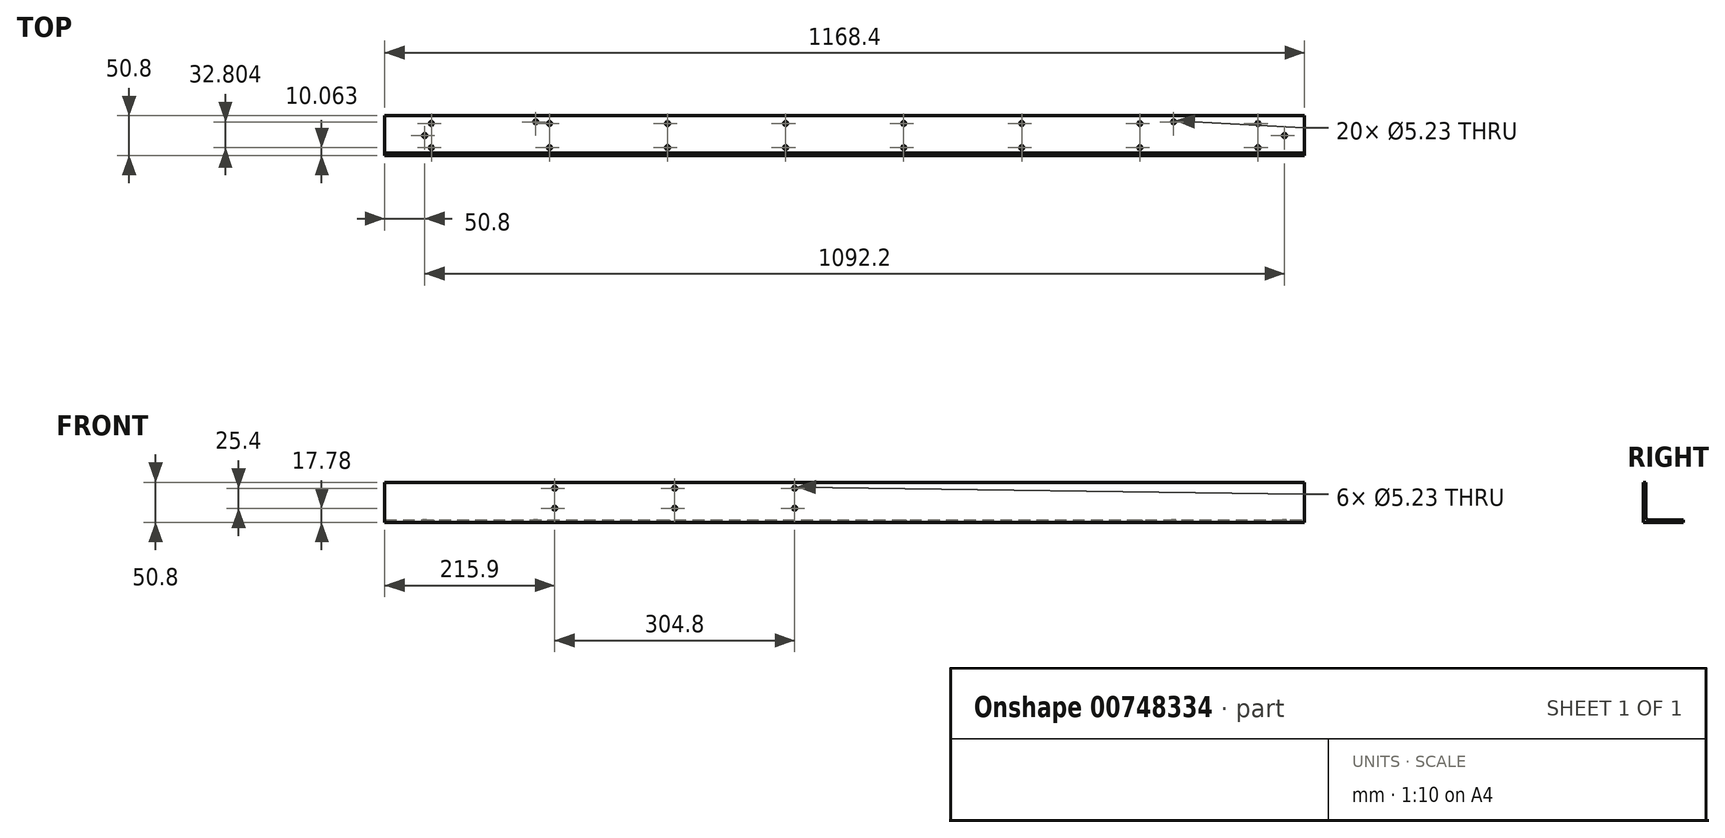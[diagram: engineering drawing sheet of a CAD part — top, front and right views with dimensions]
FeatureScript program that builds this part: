
annotation { "Feature Type Name" : "Feature", "Feature Type Description" : "" }
export const myFeature = defineFeature(function(context is Context, id is Id, definition is map)
    precondition{}
    {
        {
            var Q0;
            Q0=qCreatedBy(makeId("Right.planeOp"),FACE);
            var sketch = newSketch(context, id + "F0", { "sketchPlane" : qUnion([Q0])});
            skLineSegment(sketch, "E0", {"start": v(0, 0) * mm, "end": v(0, -44.45) * mm});
            skLineSegment(sketch, "E1", {"start": v(3.18, -47.62) * mm, "end": v(47.63, -47.62) * mm});
            skLineSegment(sketch, "E2.0", {"start": v(-3.18, -50.8) * mm, "end": v(47.63, -50.8) * mm});
            skLineSegment(sketch, "E2.1", {"start": v(-3.17, 0) * mm, "end": v(-3.18, -50.8) * mm});
            skLineSegment(sketch, "E3", {"start": v(-3.18, 0) * mm, "end": v(0, 0) * mm});
            skLineSegment(sketch, "E4", {"start": v(47.63, -47.62) * mm, "end": v(47.63, -50.8) * mm});
            skPoint(sketch, "E5.visualSharp", {"position": v(0, -47.63) * mm});
            skArc(sketch, "E5.filletArc", {"start": v(0, -44.45) * mm, "mid": v(0.93, -46.7) * mm, "end": v(3.18, -47.63) * mm});
            skSolve(sketch);
        }
        {
            var Q0;
            Q0=makeQuery(id+"F0.imprint","IMPRINT",FACE,{"disambiguationData":[TD([[makeQuery(id+"F0.imprint","IMPRINT",EDGE,{"derivedFrom":sQuery(id+"F0.wireOp",EDGE,"E0")}),-1.0]])]});
            extrude(context, id + "F1", {"entities" : qUnion([Q0]), "oppositeDirection" : true, "depth" : 1168.4 * mm, "offsetDistance" : 25.4 * mm});
        }
        {
            var Q0;
            Q0=makeQuery(id+"F1.opExtrude","SWEPT_FACE",FACE,{"disambiguationData":[OSD([sQuery(id+"F0.wireOp",EDGE,"E2.0")])]});
            var sketch = newSketch(context, id + "F2", { "sketchPlane" : qUnion([Q0])});
            skLineSegment(sketch, "E6", {"start": v(-584.2, -47.62) * mm, "end": v(-584.2, 3.17) * mm, "construction": true});
            skLineSegment(sketch, "E7", {"start": v(-1168.4, -22.22) * mm, "end": v(0, -22.22) * mm, "construction": true});
            skLineSegment(sketch, "E8.0", {"start": v(-1371.6, -37.57) * mm, "end": v(203.2, -37.57) * mm, "construction": true});
            skLineSegment(sketch, "E9.0", {"start": v(-1371.6, -6.88) * mm, "end": v(203.2, -6.88) * mm, "construction": true});
            skLineSegment(sketch, "E10.0", {"start": v(-509.2, -47.62) * mm, "end": v(-509.2, 3.17) * mm, "construction": true});
            skLineSegment(sketch, "E11.0", {"start": v(-359.2, -47.62) * mm, "end": v(-359.2, 3.17) * mm, "construction": true});
            skLineSegment(sketch, "E12.0", {"start": v(-209.2, -47.62) * mm, "end": v(-209.2, 3.17) * mm, "construction": true});
            skLineSegment(sketch, "E13.0", {"start": v(-59.2, -47.62) * mm, "end": v(-59.2, 3.17) * mm, "construction": true});
            skLineSegment(sketch, "E14.0", {"start": v(-659.2, -47.62) * mm, "end": v(-659.2, 3.17) * mm, "construction": true});
            skLineSegment(sketch, "E15.0", {"start": v(-809.2, -47.63) * mm, "end": v(-809.2, 3.17) * mm, "construction": true});
            skLineSegment(sketch, "E16.0", {"start": v(-959.2, -47.63) * mm, "end": v(-959.2, 3.17) * mm, "construction": true});
            skLineSegment(sketch, "E17.0", {"start": v(-1109.2, -47.63) * mm, "end": v(-1109.2, 3.17) * mm, "construction": true});
            skCircle(sketch, "E18", {"center": v(-1109.2, -37.57) * mm, "radius": 2.62 * mm});
            skCircle(sketch, "E19", {"center": v(-1109.2, -6.88) * mm, "radius": 2.62 * mm});
            skCircle(sketch, "E20", {"center": v(-959.2, -37.57) * mm, "radius": 2.62 * mm});
            skCircle(sketch, "E21", {"center": v(-959.2, -6.88) * mm, "radius": 2.62 * mm});
            skCircle(sketch, "E22", {"center": v(-809.2, -37.57) * mm, "radius": 2.62 * mm});
            skCircle(sketch, "E23", {"center": v(-809.2, -6.88) * mm, "radius": 2.62 * mm});
            skCircle(sketch, "E24", {"center": v(-659.2, -37.57) * mm, "radius": 2.62 * mm});
            skCircle(sketch, "E25", {"center": v(-659.2, -6.88) * mm, "radius": 2.62 * mm});
            skCircle(sketch, "E26", {"center": v(-509.2, -37.57) * mm, "radius": 2.62 * mm});
            skCircle(sketch, "E27", {"center": v(-509.2, -6.88) * mm, "radius": 2.62 * mm});
            skCircle(sketch, "E28", {"center": v(-359.2, -37.57) * mm, "radius": 2.62 * mm});
            skCircle(sketch, "E29", {"center": v(-359.2, -6.88) * mm, "radius": 2.62 * mm});
            skCircle(sketch, "E30", {"center": v(-209.2, -37.57) * mm, "radius": 2.62 * mm});
            skCircle(sketch, "E31", {"center": v(-209.2, -6.88) * mm, "radius": 2.62 * mm});
            skCircle(sketch, "E32", {"center": v(-59.2, -37.57) * mm, "radius": 2.62 * mm});
            skCircle(sketch, "E33", {"center": v(-59.2, -6.88) * mm, "radius": 2.62 * mm});
            skSolve(sketch);
        }
        {
            var Q0;
            Q0=qSketchRegion(id+"F2",true);
            extrude(context, id + "F3", {"entities" : qUnion([Q0]), "operationType" : NewBodyOperationType.REMOVE, "endBound" : BoundingType.THROUGH_ALL, "oppositeDirection" : true, "depth" : 25.4 * mm, "offsetDistance" : 25.4 * mm});
        }
        {
            var Q0;
            Q0=makeQuery(id+"F1.opExtrude","SWEPT_FACE",FACE,{"disambiguationData":[OSD([sQuery(id+"F0.wireOp",EDGE,"E1")])]});
            var sketch = newSketch(context, id + "F4", { "sketchPlane" : qUnion([Q0])});
            skLineSegment(sketch, "E34", {"start": v(-25.4, 47.63) * mm, "end": v(-25.4, 3.18) * mm, "construction": true});
            skCircle(sketch, "E35", {"center": v(-25.4, 22.23) * mm, "radius": 2.62 * mm});
            skLineSegment(sketch, "E36", {"start": v(-1117.6, 47.63) * mm, "end": v(-1117.6, 3.18) * mm, "construction": true});
            skCircle(sketch, "E37", {"center": v(-1117.6, 22.22) * mm, "radius": 2.62 * mm});
            skLineSegment(sketch, "E38", {"start": v(0, 22.23) * mm, "end": v(-1168.4, 22.22) * mm, "construction": true});
            skPoint(sketch, "E38.endSnap0", {"position": v(-1168.4, 25.4) * mm});
            skLineSegment(sketch, "E39", {"start": v(0, 39.69) * mm, "end": v(-1168.4, 39.69) * mm, "construction": true});
            skCircle(sketch, "E40", {"center": v(-166.33, 39.69) * mm, "radius": 2.62 * mm});
            skCircle(sketch, "E41", {"center": v(-976.66, 39.69) * mm, "radius": 2.62 * mm});
            skSolve(sketch);
        }
        {
            var Q0;
            Q0=qSketchRegion(id+"F4",true);
            extrude(context, id + "F5", {"entities" : qUnion([Q0]), "operationType" : NewBodyOperationType.REMOVE, "endBound" : BoundingType.THROUGH_ALL, "oppositeDirection" : true, "depth" : 25.4 * mm, "offsetDistance" : 25.4 * mm});
        }
        {
            var Q0;
            Q0=makeQuery(id+"F1.opExtrude","SWEPT_FACE",FACE,{"disambiguationData":[OSD([sQuery(id+"F0.wireOp",EDGE,"E2.1")])]});
            var sketch = newSketch(context, id + "F6", { "sketchPlane" : qUnion([Q0])});
            skLineSegment(sketch, "E42", {"start": v(-1168.4, -7.62) * mm, "end": v(0, -7.62) * mm, "construction": true});
            skLineSegment(sketch, "E43", {"start": v(-952.5, 0) * mm, "end": v(-952.5, -50.8) * mm, "construction": true});
            skLineSegment(sketch, "E44.0", {"start": v(-800.1, 3.5) * mm, "end": v(-800.1, -47.3) * mm, "construction": true});
            skLineSegment(sketch, "E45.0", {"start": v(-647.7, 3.5) * mm, "end": v(-647.7, -47.3) * mm, "construction": true});
            skCircle(sketch, "E46", {"center": v(-952.5, -7.62) * mm, "radius": 2.62 * mm});
            skCircle(sketch, "E47", {"center": v(-800.1, -7.62) * mm, "radius": 2.62 * mm});
            skCircle(sketch, "E48", {"center": v(-647.7, -7.62) * mm, "radius": 2.62 * mm});
            skLineSegment(sketch, "E49", {"start": v(0, -33.02) * mm, "end": v(-1168.4, -33.02) * mm, "construction": true});
            skCircle(sketch, "E50", {"center": v(-952.5, -33.02) * mm, "radius": 2.62 * mm});
            skCircle(sketch, "E51", {"center": v(-800.1, -33.02) * mm, "radius": 2.62 * mm});
            skCircle(sketch, "E52", {"center": v(-647.7, -33.02) * mm, "radius": 2.62 * mm});
            skSolve(sketch);
        }
        {
            var Q0;
            Q0 = qSketchRegion(id + "F6", true);
            extrude(context, id + "F7", {"entities" : qUnion([Q0]), "operationType" : NewBodyOperationType.REMOVE, "endBound" : BoundingType.THROUGH_ALL, "oppositeDirection" : true, "depth" : 25.4 * mm, "offsetDistance" : 25.4 * mm});
        }
    });
